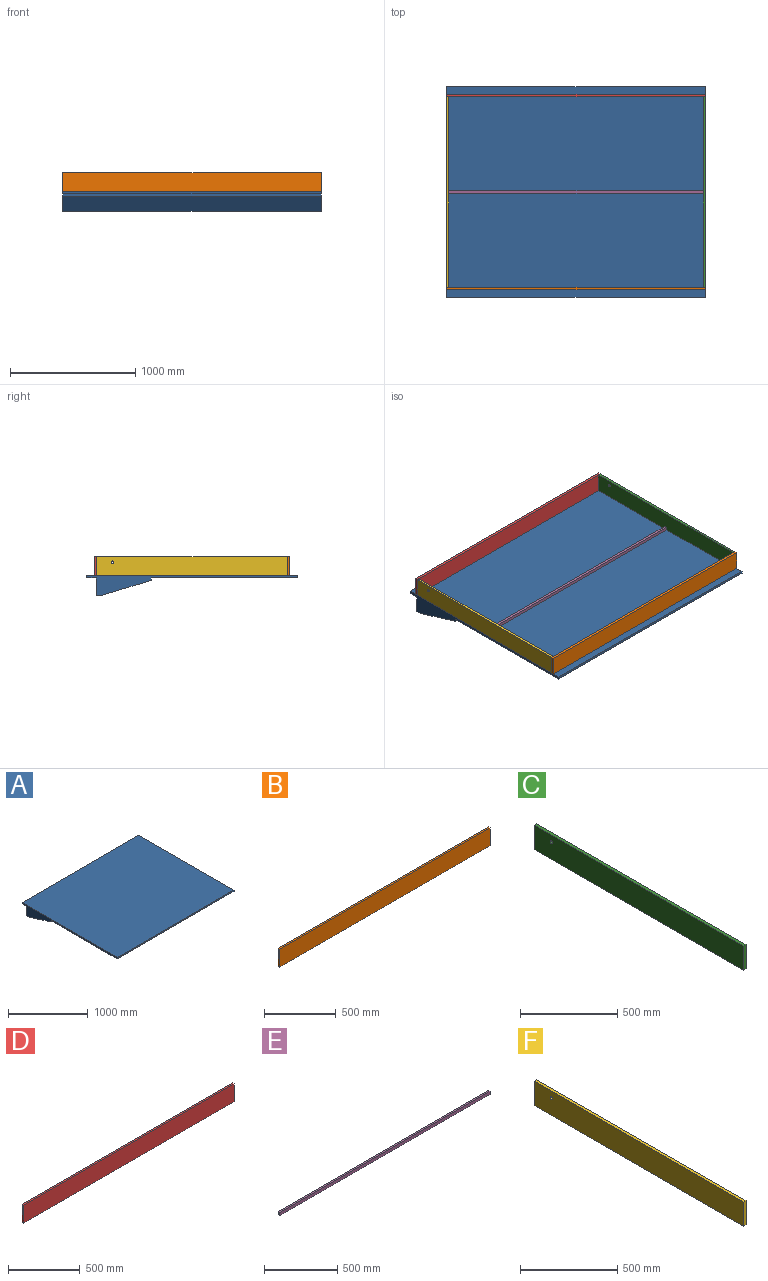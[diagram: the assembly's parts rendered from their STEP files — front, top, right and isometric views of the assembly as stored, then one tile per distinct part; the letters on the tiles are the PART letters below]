
ASSEMBLY  parts=6 mates=7
PART A: 11 faces, bbox 2070.1x1683.2x158.8 mm
  f0: plane 1683.24x158.75mm, normal (1,0,0), area 69564.5mm2, adj f1,f2,f4,f5,f6,f7,f8,f9
  f1: plane 2070.1x19.05mm, normal (0,-1,0), area 39435.4mm2, adj f0,f3,f6,f8
  f2: plane 2070.1x44.45mm, normal (0,0,-1), area 92015.9mm2, adj f0,f3,f7,f8
  f3: plane 1683.24x158.75mm, normal (-1,0,0), area 69564.5mm2, adj f1,f2,f4,f5,f6,f7,f8,f9
  f4: plane 2070.1x19.05mm, normal (0,-1,0), area 39435.4mm2, adj f0,f3,f5,f6
  f5: plane 2070.1x1683.24mm, normal (0,0,1), area 3484481.2mm2, adj f0,f3,f4,f9
  f6: plane 2070.1x1168.4mm, normal (0,0,-1), area 2418704.8mm2, adj f0,f1,f3,f4
  f7: plane 2070.1x139.7mm, normal (0,1,0), area 289193mm2, adj f0,f2,f3,f10
  f8: plane 2070.1x394.19mm, normal (0,-0.29,-0.96), area 853384.8mm2, adj f0,f1,f2,f3
  f9: plane 2070.1x19.05mm, normal (0,1,0), area 39435.4mm2, adj f0,f3,f5,f10
  f10: plane 2070.1x76.2mm, normal (0,0,-1), area 157741.6mm2, adj f0,f3,f7,f9
PART B: 6 faces, bbox 2070.1x19.1x152.4 mm
  f0: plane 2070.1x152.4mm, normal (0,1,0), area 315483.2mm2, adj f1,f3,f4,f5
  f1: plane 152.4x19.05mm, normal (-1,0,0), area 2903.2mm2, adj f0,f2,f4,f5
  f2: plane 2070.1x152.4mm, normal (0,-1,0), area 315483.2mm2, adj f1,f3,f4,f5
  f3: plane 152.4x19.05mm, normal (1,0,0), area 2903.2mm2, adj f0,f2,f4,f5
  f4: plane 2070.1x19.05mm, normal (0,0,1), area 39435.4mm2, adj f0,f1,f2,f3
  f5: plane 2070.1x19.05mm, normal (0,0,-1), area 39435.4mm2, adj f0,f1,f2,f3
PART C: 7 faces, bbox 19.1x1524x152.4 mm
  f0: plane 1524x152.4mm, normal (-1,0,0), area 231972.6mm2, adj f1,f3,f4,f5,f6
  f1: plane 152.4x19.05mm, normal (0,-1,0), area 2903.2mm2, adj f0,f2,f4,f5
  f2: plane 1524x152.4mm, normal (1,0,0), area 231972.6mm2, adj f1,f3,f4,f5,f6
  f3: plane 152.4x19.05mm, normal (0,1,0), area 2903.2mm2, adj f0,f2,f4,f5
  f4: plane 1524x19.05mm, normal (0,0,1), area 29032.2mm2, adj f0,f1,f2,f3
  f5: plane 1524x19.05mm, normal (0,0,-1), area 29032.2mm2, adj f0,f1,f2,f3
  f6: cylinder r=9.53mm len=19.05mm, axis (1,0,0), area 1140.1mm2, adj f0,f2
PART D: 6 faces, bbox 2070.1x19.1x152.4 mm
  f0: plane 2070.1x152.4mm, normal (0,-1,0), area 315483.2mm2, adj f1,f3,f4,f5
  f1: plane 152.4x19.05mm, normal (1,0,0), area 2903.2mm2, adj f0,f2,f4,f5
  f2: plane 2070.1x152.4mm, normal (0,1,0), area 315483.2mm2, adj f1,f3,f4,f5
  f3: plane 152.4x19.05mm, normal (-1,0,0), area 2903.2mm2, adj f0,f2,f4,f5
  f4: plane 2070.1x19.05mm, normal (0,0,1), area 39435.4mm2, adj f0,f1,f2,f3
  f5: plane 2070.1x19.05mm, normal (0,0,-1), area 39435.4mm2, adj f0,f1,f2,f3
PART E: 6 faces, bbox 2032x19.1x25.4 mm
  f0: plane 2032x25.4mm, normal (0,-1,0), area 51612.8mm2, adj f1,f3,f4,f5
  f1: plane 25.4x19.05mm, normal (1,0,0), area 483.9mm2, adj f0,f2,f4,f5
  f2: plane 2032x25.4mm, normal (0,1,0), area 51612.8mm2, adj f1,f3,f4,f5
  f3: plane 25.4x19.05mm, normal (-1,0,0), area 483.9mm2, adj f0,f2,f4,f5
  f4: plane 2032x19.05mm, normal (0,0,1), area 38709.6mm2, adj f0,f1,f2,f3
  f5: plane 2032x19.05mm, normal (0,0,-1), area 38709.6mm2, adj f0,f1,f2,f3
PART F: 7 faces, bbox 19.1x1524x152.4 mm
  f0: plane 1524x152.4mm, normal (1,0,0), area 231972.6mm2, adj f1,f3,f4,f5,f6
  f1: plane 152.4x19.05mm, normal (0,1,0), area 2903.2mm2, adj f0,f2,f4,f5
  f2: plane 1524x152.4mm, normal (-1,0,0), area 231972.6mm2, adj f1,f3,f4,f5,f6
  f3: plane 152.4x19.05mm, normal (0,-1,0), area 2903.2mm2, adj f0,f2,f4,f5
  f4: plane 1524x19.05mm, normal (0,0,1), area 29032.2mm2, adj f0,f1,f2,f3
  f5: plane 1524x19.05mm, normal (0,0,-1), area 29032.2mm2, adj f0,f1,f2,f3
  f6: cylinder r=9.53mm len=19.05mm, axis (1,0,0), area 1140.1mm2, adj f0,f2
PLACE A t=(-268.09,165.07,-259.42)mm
PLACE B t=(-268.09,225.64,-259.42)mm
PLACE C t=(-268.09,225.64,-259.42)mm
PLACE D t=(-268.09,225.64,-259.42)mm
PLACE E t=(-268.09,225.64,-259.42)mm
PLACE F t=(-268.09,225.64,-259.42)mm
MATE fastened D.f0 <-> F.f1  axis (0,-1,0) through (-1303.14,288.65,305.73)mm
MATE fastened B.f0 <-> C.f1  axis (0,1,0) through (766.96,-1235.35,305.73)mm
MATE fastened E.f3 <-> F.f0  axis (-1,0,0) through (-1284.09,-473.35,229.53)mm
MATE fastened B.f0 <-> F.f3  axis (0,1,0) through (-1303.14,-1235.35,305.73)mm
MATE fastened C.f3 <-> D.f0  axis (0,1,0) through (766.96,288.65,305.73)mm
MATE fastened A.f5 <-> E.f5  axis (0,0,1) through (-268.09,-473.35,229.53)mm
MATE fastened C.f0 <-> E.f1  axis (-1,0,0) through (747.91,-473.35,229.53)mm
